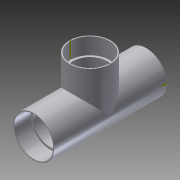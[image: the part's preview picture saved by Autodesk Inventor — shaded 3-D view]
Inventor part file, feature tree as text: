
AUTODESK INVENTOR PART (.ipt)
format: ipt  version: 2014 (Build 180170000, 170)  size: 199,168 bytes
history: native  units: in
note: dims shown in document units (in); Inventor stores cm internally (conversion verified against a paired STEP export)
features: sketch x10, extrude x9, plane x2
ambient origin geometry x8: Origin, YZ Plane, XZ Plane, XY Plane, X Axis, Y Axis, Z Axis, Center Point
bodies: Solid1 (feature_tree)
feature tree (21):
  extrude  "mainBody"  Depth=6.875in TaperAngle=0.0deg
  sketch  "Sketch10"  dims[d29=3.4375in d30=2.5in]
  plane  "Work Plane5"
  extrude  "TBody"  Depth=2.5in
  extrude  "TSocket"  Depth=1.25in
  extrude  "TTube"  Depth=1.0in
  extrude  "mainTube"  Depth=1.5in
  extrude  "mainSocket1"  Depth=2.375in
  extrude  "mainSocket2"  Depth=1.0in
  extrude  "Extrusion20"  Depth=0.1in
  plane  "Work Plane6"
  extrude  "Extrusion22"  Depth=0.1in
  sketch  "Sketch1"  dims[d0=2.5in d1=6.875in d2=0.0in]
  sketch  "Sketch11"  dims[d31=1.5in d32=1.25in d33=0.0in d34=0.0in d35=2.375in]
  sketch  "Sketch12"  dims[d37=1.0in d38=0.0in d39=2.1in]
  sketch  "Sketch13"  dims[d41=1.5in d42=0.0in d43=2.1in]
  sketch  "Sketch14"  dims[d45=7.0in d46=0.0in d47=2.375in]
  sketch  "Sketch15"  dims[d49=1.0in d50=0.0in d51=2.375in]
  sketch  "Sketch16"  dims[d53=1.0in d54=0.0in d72=0.1in]
  sketch  "Sketch24"  dims[d73=1.0in d74=0.0in d75=0.1in]
  sketch  "Sketch27"  dims[d76=1.24in d79=1.0in d80=0.0in]
